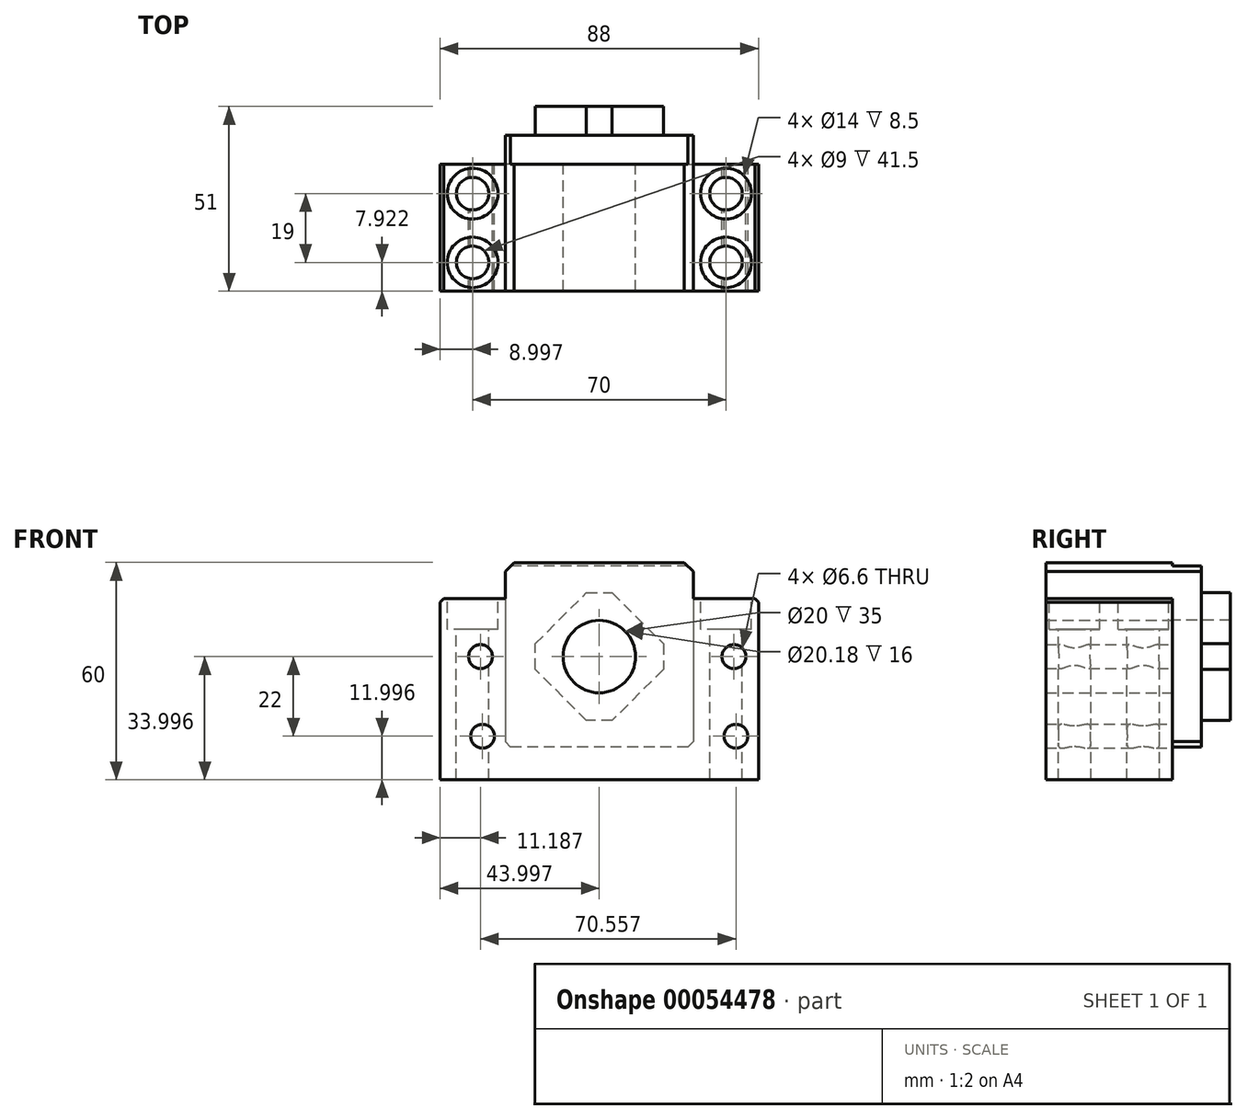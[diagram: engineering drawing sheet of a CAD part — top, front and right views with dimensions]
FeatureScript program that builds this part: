
annotation { "Feature Type Name" : "Feature", "Feature Type Description" : "" }
export const myFeature = defineFeature(function(context is Context, id is Id, definition is map)
    precondition{}
    {
        {
            var Q0;
            Q0=qCreatedBy(makeId("Front.planeOp"),FACE);
            var sketch = newSketch(context, id + "F0", { "sketchPlane" : qUnion([Q0])});
            skLineSegment(sketch, "E0.bottom", {"start": v(-37.23, 17.93) * mm, "end": v(-21.73, 17.93) * mm});
            skLineSegment(sketch, "E0.top", {"start": v(-39.73, -32.07) * mm, "end": v(48.27, -32.07) * mm});
            skLineSegment(sketch, "E0.left", {"start": v(-39.73, 15.43) * mm, "end": v(-39.73, -32.07) * mm});
            skLineSegment(sketch, "E0.right", {"start": v(48.27, 15.43) * mm, "end": v(48.27, -32.07) * mm});
            skCircle(sketch, "E1", {"center": v(4.27, 1.93) * mm, "radius": 10 * mm});
            skLineSegment(sketch, "E2.bottom", {"start": v(-21.73, 27.93) * mm, "end": v(30.27, 27.93) * mm});
            skLineSegment(sketch, "E2.left", {"start": v(-21.73, 27.93) * mm, "end": v(-21.73, 17.93) * mm});
            skLineSegment(sketch, "E2.right", {"start": v(30.27, 27.93) * mm, "end": v(30.27, 17.93) * mm});
            skLineSegment(sketch, "E3.trimOffspring", {"start": v(30.27, 17.93) * mm, "end": v(45.77, 17.93) * mm});
            skCircle(sketch, "E4", {"center": v(-28.54, 1.93) * mm, "radius": 3.3 * mm});
            skCircle(sketch, "E5", {"center": v(-27.99, -20.07) * mm, "radius": 3.3 * mm});
            skCircle(sketch, "E6", {"center": v(42.01, -20.07) * mm, "radius": 3.3 * mm});
            skCircle(sketch, "E7", {"center": v(41.46, 1.93) * mm, "radius": 3.3 * mm});
            skLineSegment(sketch, "E8.top", {"start": v(-39.73, 17.93) * mm, "end": v(-33.45, 17.93) * mm});
            skLineSegment(sketch, "E8.left", {"start": v(-39.73, 9.55) * mm, "end": v(-39.73, 17.93) * mm});
            skLineSegment(sketch, "E9.bottom", {"start": v(42.4, 17.93) * mm, "end": v(48.27, 17.93) * mm});
            skLineSegment(sketch, "E9.right", {"start": v(48.27, 17.93) * mm, "end": v(48.27, 11.22) * mm});
            skSolve(sketch);
        }
        {
            var Q0;
            {var subQ0=sQuery(id+"F0.wireOp",EDGE,"E0.bottom");Q0=makeQuery(id+"F0.imprint","IMPRINT",FACE,{"disambiguationData":[TD([[makeQuery(id+"F0.imprint","IMPRINT",EDGE,{"derivedFrom":subQ0}),-1.0]])]});}
            extrude(context, id + "F1", {"entities" : qUnion([Q0]), "depth" : 35 * mm});
        }
        {
            var Q0;
            Q0=makeQuery(id+"F1.opExtrude","SWEPT_EDGE",EDGE,{"disambiguationData":[OSD([sQuery(id+"F0.wireOp",EDGE,"E2.bottom"),sQuery(id+"F0.wireOp",EDGE,"E2.left")])]});
            var Q1;
            Q1=makeQuery(id+"F1.opExtrude","SWEPT_EDGE",EDGE,{"disambiguationData":[OSD([sQuery(id+"F0.wireOp",EDGE,"E2.bottom"),sQuery(id+"F0.wireOp",EDGE,"E2.right")])]});
            chamfer(context, id + "F2", {"entities" : qUnion([Q0, Q1]), "width" : 2.5 * mm, "tangentPropagation" : true});
        }
        {
            var Q0;
            Q0=makeQuery(id+"F1.opExtrude","SWEPT_FACE",FACE,{"disambiguationData":[OSD([sQuery(id+"F0.wireOp",EDGE,"E0.bottom")])]});
            var sketch = newSketch(context, id + "F3", { "sketchPlane" : qUnion([Q0])});
            skCircle(sketch, "E10", {"center": v(39.27, -27.08) * mm, "radius": 7 * mm});
            skCircle(sketch, "E11", {"center": v(-30.73, -8.08) * mm, "radius": 4.5 * mm});
            skCircle(sketch, "E12", {"center": v(39.27, -8.08) * mm, "radius": 7 * mm});
            skCircle(sketch, "E13", {"center": v(39.27, -27.08) * mm, "radius": 4.5 * mm});
            skCircle(sketch, "E14", {"center": v(-30.73, -27.08) * mm, "radius": 4.5 * mm});
            skCircle(sketch, "E15", {"center": v(39.27, -8.08) * mm, "radius": 4.5 * mm});
            skCircle(sketch, "E16", {"center": v(-30.73, -8.08) * mm, "radius": 7 * mm});
            skCircle(sketch, "E17", {"center": v(-30.73, -27.08) * mm, "radius": 7 * mm});
            skSolve(sketch);
        }
        {
            var Q0;
            Q0=makeQuery(id+"F3.imprint","IMPRINT",FACE,{"disambiguationData":[TD([[makeQuery(id+"F3.imprint","IMPRINT",EDGE,{"derivedFrom":sQuery(id+"F3.wireOp",EDGE,"E10")}),1.0]])]});
            var Q1;
            Q1=makeQuery(id+"F3.imprint","IMPRINT",FACE,{"disambiguationData":[TD([[makeQuery(id+"F3.imprint","IMPRINT",EDGE,{"derivedFrom":sQuery(id+"F3.wireOp",EDGE,"E12")}),1.0]])]});
            var Q2;
            Q2=makeQuery(id+"F3.imprint","IMPRINT",FACE,{"disambiguationData":[TD([[makeQuery(id+"F3.imprint","IMPRINT",EDGE,{"derivedFrom":sQuery(id+"F3.wireOp",EDGE,"E11")}),-1.0]])]});
            var Q3;
            Q3=makeQuery(id+"F3.imprint","IMPRINT",FACE,{"disambiguationData":[TD([[makeQuery(id+"F3.imprint","IMPRINT",EDGE,{"derivedFrom":sQuery(id+"F3.wireOp",EDGE,"E14")}),-1.0]])]});
            extrude(context, id + "F4", {"entities" : qUnion([Q0, Q1, Q2, Q3]), "operationType" : NewBodyOperationType.REMOVE, "oppositeDirection" : true, "depth" : 8.5 * mm});
        }
        {
            var Q0;
            Q0=makeQuery(id+"F4.boolean.opBoolean","SPLIT",FACE,{"disambiguationData":[TD([makeQuery(id+"F4.opExtrude","SWEPT_FACE",FACE,{"disambiguationData":[OSD([sQuery(id+"F3.wireOp",EDGE,"E13")])]})])],"derivedFrom":makeQuery(id+"F1.opExtrude","SWEPT_FACE",FACE,{"disambiguationData":[OSD([sQuery(id+"F0.wireOp",EDGE,"E3.trimOffspring"),sQuery(id+"F0.wireOp",EDGE,"E9.bottom")])]})});
            var Q1;
            Q1=makeQuery(id+"F4.boolean.opBoolean","SPLIT",FACE,{"disambiguationData":[TD([makeQuery(id+"F4.opExtrude","SWEPT_FACE",FACE,{"disambiguationData":[OSD([sQuery(id+"F3.wireOp",EDGE,"E15")])]})])],"derivedFrom":makeQuery(id+"F1.opExtrude","SWEPT_FACE",FACE,{"disambiguationData":[OSD([sQuery(id+"F0.wireOp",EDGE,"E3.trimOffspring"),sQuery(id+"F0.wireOp",EDGE,"E9.bottom")])]})});
            var Q2;
            Q2=makeQuery(id+"F4.boolean.opBoolean","SPLIT",FACE,{"disambiguationData":[TD([makeQuery(id+"F4.opExtrude","SWEPT_FACE",FACE,{"disambiguationData":[OSD([sQuery(id+"F3.wireOp",EDGE,"E11")])]})])],"derivedFrom":makeQuery(id+"F1.opExtrude","SWEPT_FACE",FACE,{"disambiguationData":[OSD([sQuery(id+"F0.wireOp",EDGE,"E0.bottom"),sQuery(id+"F0.wireOp",EDGE,"E8.top")])]})});
            var Q3;
            Q3=makeQuery(id+"F4.boolean.opBoolean","SPLIT",FACE,{"disambiguationData":[TD([makeQuery(id+"F4.opExtrude","SWEPT_FACE",FACE,{"disambiguationData":[OSD([sQuery(id+"F3.wireOp",EDGE,"E14")])]})])],"derivedFrom":makeQuery(id+"F1.opExtrude","SWEPT_FACE",FACE,{"disambiguationData":[OSD([sQuery(id+"F0.wireOp",EDGE,"E0.bottom"),sQuery(id+"F0.wireOp",EDGE,"E8.top")])]})});
            extrude(context, id + "F5", {"entities" : qUnion([Q0, Q1, Q2, Q3]), "operationType" : NewBodyOperationType.REMOVE, "endBound" : BoundingType.THROUGH_ALL, "oppositeDirection" : true, "depth" : 25 * mm});
        }
        {
            var Q0;
            Q0=makeQuery(id+"F1.opExtrude","SWEPT_EDGE",EDGE,{"disambiguationData":[OSD([sQuery(id+"F0.wireOp",EDGE,"E9.bottom"),sQuery(id+"F0.wireOp",EDGE,"E9.right")])]});
            var Q1;
            Q1=makeQuery(id+"F1.opExtrude","SWEPT_EDGE",EDGE,{"disambiguationData":[OSD([sQuery(id+"F0.wireOp",EDGE,"E8.top"),sQuery(id+"F0.wireOp",EDGE,"E8.left")])]});
            chamfer(context, id + "F6", {"entities" : qUnion([Q0, Q1]), "width" : 1 * mm, "tangentPropagation" : true});
        }
        {
            var Q0;
            Q0=makeQuery(id+"F1.opExtrude","CAP_FACE",FACE,{"disambiguationData":[OSD([sQuery(id+"F0.wireOp",EDGE,"E0.bottom"),sQuery(id+"F0.wireOp",EDGE,"E0.top"),sQuery(id+"F0.wireOp",EDGE,"E0.left"),sQuery(id+"F0.wireOp",EDGE,"E0.right"),sQuery(id+"F0.wireOp",EDGE,"E1"),sQuery(id+"F0.wireOp",EDGE,"E2.bottom"),sQuery(id+"F0.wireOp",EDGE,"E2.left"),sQuery(id+"F0.wireOp",EDGE,"E2.right"),sQuery(id+"F0.wireOp",EDGE,"E3.trimOffspring"),sQuery(id+"F0.wireOp",EDGE,"E4"),sQuery(id+"F0.wireOp",EDGE,"E5"),sQuery(id+"F0.wireOp",EDGE,"E6"),sQuery(id+"F0.wireOp",EDGE,"E7"),sQuery(id+"F0.wireOp",EDGE,"E8.top"),sQuery(id+"F0.wireOp",EDGE,"E8.left"),sQuery(id+"F0.wireOp",EDGE,"E9.bottom"),sQuery(id+"F0.wireOp",EDGE,"E9.right")])],"isStart":true});
            var sketch = newSketch(context, id + "F7", { "sketchPlane" : qUnion([Q0])});
            skLineSegment(sketch, "E18.bottom", {"start": v(-30.27, 26.93) * mm, "end": v(21.73, 26.93) * mm});
            skLineSegment(sketch, "E18.top", {"start": v(-30.27, -23.07) * mm, "end": v(21.73, -23.07) * mm});
            skLineSegment(sketch, "E18.left", {"start": v(-30.27, 26.93) * mm, "end": v(-30.27, -23.07) * mm});
            skLineSegment(sketch, "E18.right", {"start": v(21.73, 26.93) * mm, "end": v(21.73, -23.07) * mm});
            skCircle(sketch, "E19", {"center": v(-4.27, 1.93) * mm, "radius": 10.09 * mm});
            skSolve(sketch);
        }
        {
            var Q0;
            Q0 = qSketchRegion(id + "F7", true);
            extrude(context, id + "F8", {"entities" : qUnion([Q0]), "operationType" : NewBodyOperationType.ADD, "depth" : 8 * mm});
        }
        {
            var Q0;
            Q0=makeQuery(id+"F8.opExtrude","SWEPT_EDGE",EDGE,{"disambiguationData":[OSD([sQuery(id+"F7.wireOp",EDGE,"E18.bottom"),sQuery(id+"F7.wireOp",EDGE,"E18.left")])]});
            chamfer(context, id + "F9", {"entities" : qUnion([Q0]), "width" : 1.5 * mm, "tangentPropagation" : true});
        }
        {
            var Q0;
            Q0=makeQuery(id+"F8.opExtrude","SWEPT_EDGE",EDGE,{"disambiguationData":[OSD([sQuery(id+"F7.wireOp",EDGE,"E18.bottom"),sQuery(id+"F7.wireOp",EDGE,"E18.right")])]});
            var Q1;
            Q1=makeQuery(id+"F8.opExtrude","SWEPT_EDGE",EDGE,{"disambiguationData":[OSD([sQuery(id+"F7.wireOp",EDGE,"E18.top"),sQuery(id+"F7.wireOp",EDGE,"E18.left")])]});
            var Q2;
            Q2=makeQuery(id+"F8.opExtrude","SWEPT_EDGE",EDGE,{"disambiguationData":[OSD([sQuery(id+"F7.wireOp",EDGE,"E18.top"),sQuery(id+"F7.wireOp",EDGE,"E18.right")])]});
            chamfer(context, id + "F10", {"entities" : qUnion([Q0, Q1, Q2]), "width" : 1.5 * mm, "tangentPropagation" : true});
        }
        {
            var Q0;
            Q0=makeQuery(id+"F8.opExtrude","CAP_FACE",FACE,{"disambiguationData":[OSD([sQuery(id+"F7.wireOp",EDGE,"E18.bottom"),sQuery(id+"F7.wireOp",EDGE,"E18.top"),sQuery(id+"F7.wireOp",EDGE,"E18.left"),sQuery(id+"F7.wireOp",EDGE,"E18.right"),sQuery(id+"F7.wireOp",EDGE,"E19")])],"isStart":false});
            var sketch = newSketch(context, id + "F11", { "sketchPlane" : qUnion([Q0])});
            skLineSegment(sketch, "E20", {"start": v(-25.48, 1.93) * mm, "end": v(-4.27, -19.29) * mm});
            skLineSegment(sketch, "E21", {"start": v(-4.27, -19.29) * mm, "end": v(16.95, 1.93) * mm});
            skLineSegment(sketch, "E22", {"start": v(16.95, 1.93) * mm, "end": v(-4.27, 23.14) * mm});
            skLineSegment(sketch, "E23", {"start": v(-4.27, 23.14) * mm, "end": v(-25.48, 1.93) * mm});
            skSolve(sketch);
        }
        {
            var Q0;
            Q0=makeQuery(id+"F11.imprint","IMPRINT",FACE,{"disambiguationData":[TD([[makeQuery(id+"F11.imprint","IMPRINT",EDGE,{"derivedFrom":sQuery(id+"F11.wireOp",EDGE,"E20")}),1.0]])]});
            extrude(context, id + "F12", {"entities" : qUnion([Q0]), "operationType" : NewBodyOperationType.ADD, "depth" : 8 * mm});
        }
        {
            var Q0;
            Q0=makeQuery(id+"F12.opExtrude","SWEPT_EDGE",EDGE,{"disambiguationData":[OSD([sQuery(id+"F11.wireOp",EDGE,"E22"),sQuery(id+"F11.wireOp",EDGE,"E23")])]});
            var Q1;
            Q1=makeQuery(id+"F12.opExtrude","SWEPT_EDGE",EDGE,{"disambiguationData":[OSD([sQuery(id+"F11.wireOp",EDGE,"E20"),sQuery(id+"F11.wireOp",EDGE,"E23")])]});
            var Q2;
            Q2=makeQuery(id+"F12.opExtrude","SWEPT_EDGE",EDGE,{"disambiguationData":[OSD([sQuery(id+"F11.wireOp",EDGE,"E20"),sQuery(id+"F11.wireOp",EDGE,"E21")])]});
            var Q3;
            Q3=makeQuery(id+"F12.opExtrude","SWEPT_EDGE",EDGE,{"disambiguationData":[OSD([sQuery(id+"F11.wireOp",EDGE,"E21"),sQuery(id+"F11.wireOp",EDGE,"E22")])]});
            chamfer(context, id + "F13", {"entities" : qUnion([Q0, Q1, Q2, Q3]), "width" : 5 * mm, "tangentPropagation" : true});
        }
    });
